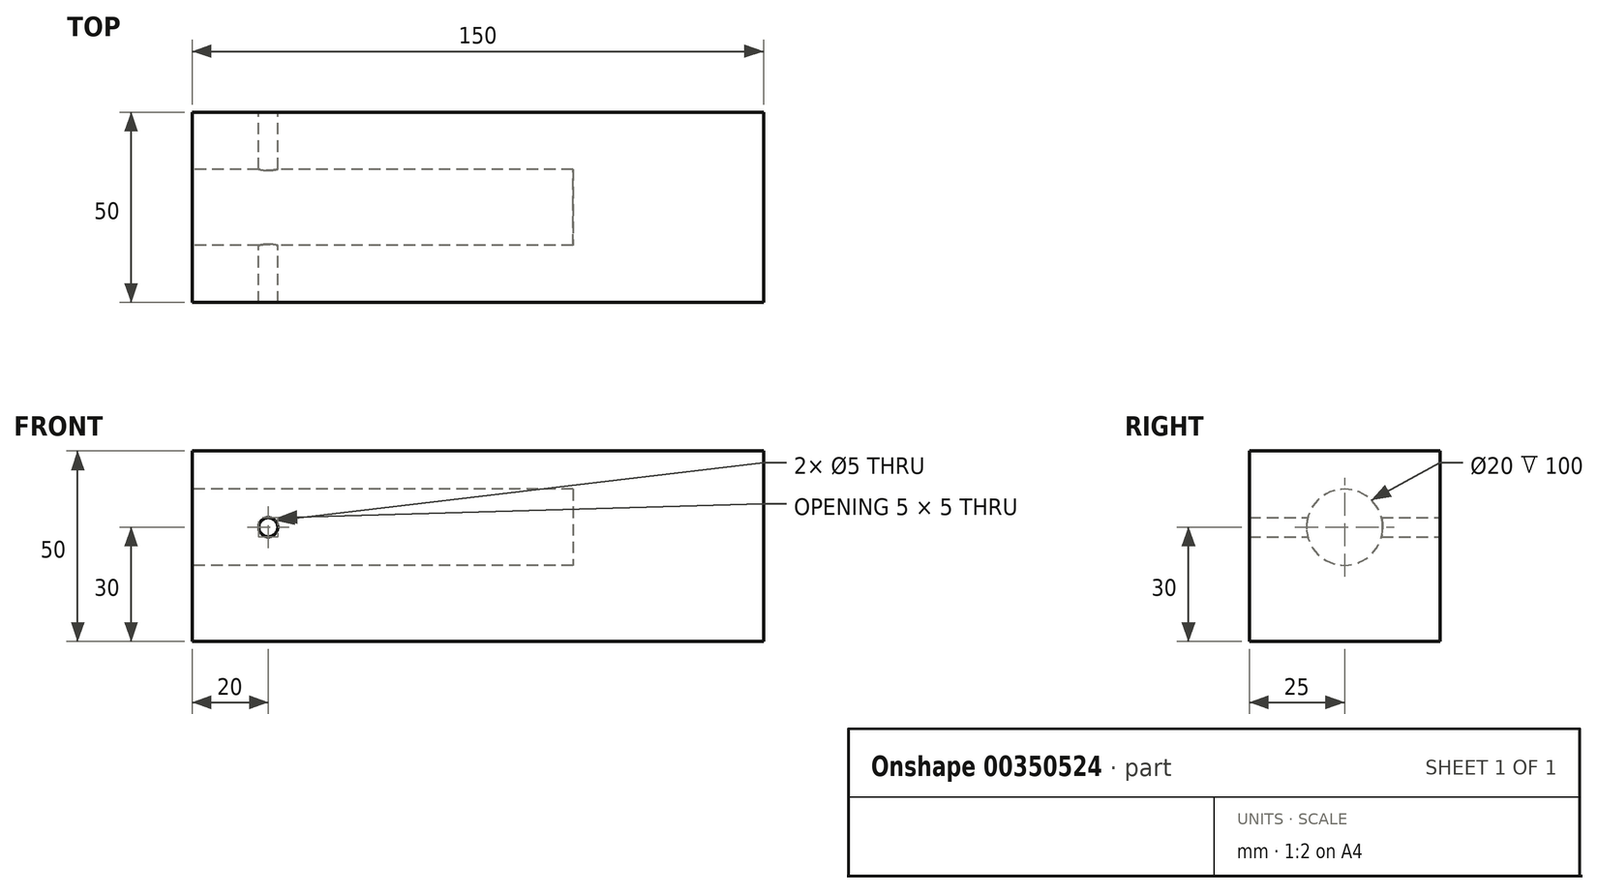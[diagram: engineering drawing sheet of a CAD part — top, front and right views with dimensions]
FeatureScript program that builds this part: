
annotation { "Feature Type Name" : "Feature", "Feature Type Description" : "" }
export const myFeature = defineFeature(function(context is Context, id is Id, definition is map)
    precondition{}
    {
        {
            var Q0;
            Q0=qCreatedBy(makeId("Front.planeOp"),FACE);
            var sketch = newSketch(context, id + "F0", { "sketchPlane" : qUnion([Q0])});
            skLineSegment(sketch, "E0.bottom", {"start": v(-50, 0) * mm, "end": v(100, 0) * mm});
            skLineSegment(sketch, "E0.top", {"start": v(-50, 50) * mm, "end": v(100, 50) * mm});
            skLineSegment(sketch, "E0.left", {"start": v(-50, 0) * mm, "end": v(-50, 50) * mm});
            skLineSegment(sketch, "E0.right", {"start": v(100, 0) * mm, "end": v(100, 50) * mm});
            skSolve(sketch);
        }
        {
            var Q0;
            Q0 = qSketchRegion(id + "F0", true);
            extrude(context, id + "F1", {"entities" : qUnion([Q0]), "depth" : 50 * mm});
        }
        {
            var Q0;
            Q0=qCreatedBy(makeId("Front.planeOp"),FACE);
            var sketch = newSketch(context, id + "F2", { "sketchPlane" : qUnion([Q0])});
            skCircle(sketch, "E1", {"center": v(-30, 30) * mm, "radius": 2.5 * mm});
            skSolve(sketch);
        }
        {
            var Q0;
            Q0=makeQuery(id+"F2.imprint","IMPRINT",FACE,{"disambiguationData":[TD([[makeQuery(id+"F2.imprint","IMPRINT",EDGE,{"derivedFrom":sQuery(id+"F2.wireOp",EDGE,"E1")}),1.0]])]});
            extrude(context, id + "F3", {"entities" : qUnion([Q0]), "operationType" : NewBodyOperationType.REMOVE, "depth" : 50 * mm});
        }
        {
            var Q0;
            Q0=makeQuery(id+"F1.opExtrude","SWEPT_FACE",FACE,{"disambiguationData":[OSD([sQuery(id+"F0.wireOp",EDGE,"E0.left")])]});
            var sketch = newSketch(context, id + "F4", { "sketchPlane" : qUnion([Q0])});
            skCircle(sketch, "E2", {"center": v(25, 30) * mm, "radius": 10 * mm});
            skSolve(sketch);
        }
        {
            var Q0;
            Q0=makeQuery(id+"F4.imprint","IMPRINT",FACE,{"disambiguationData":[TD([[makeQuery(id+"F4.imprint","IMPRINT",EDGE,{"derivedFrom":sQuery(id+"F4.wireOp",EDGE,"E2")}),1.0]])]});
            extrude(context, id + "F5", {"entities" : qUnion([Q0]), "operationType" : NewBodyOperationType.REMOVE, "oppositeDirection" : true, "depth" : 100 * mm});
        }
    });
